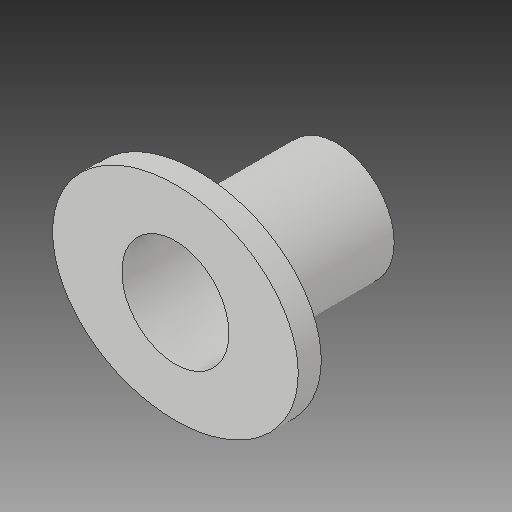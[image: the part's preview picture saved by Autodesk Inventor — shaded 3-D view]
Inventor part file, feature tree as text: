
AUTODESK INVENTOR PART (.ipt)
format: ipt  version: 2018 (Build 220112000, 112)  size: 106,496 bytes
history: native  units: mm
features: sketch x4, other x3
ambient origin geometry x8: Origin, YZ Plane, XZ Plane, XY Plane, X Axis, Y Axis, Z Axis, Center Point
bodies: Solid1 (feature_tree)
feature tree (7):
  other  "Pushfit-adapter-cap_MIR.ipt"
  other  "Solid1::Pushfit-adapter-cap_MIR.ipt"
  other  "TaggingFeature1"
  sketch  "Sketch1"  dims[d0=10.0mm]
  sketch  "Sketch2"
  sketch  "Sketch3"
  sketch  "Sketch4"
